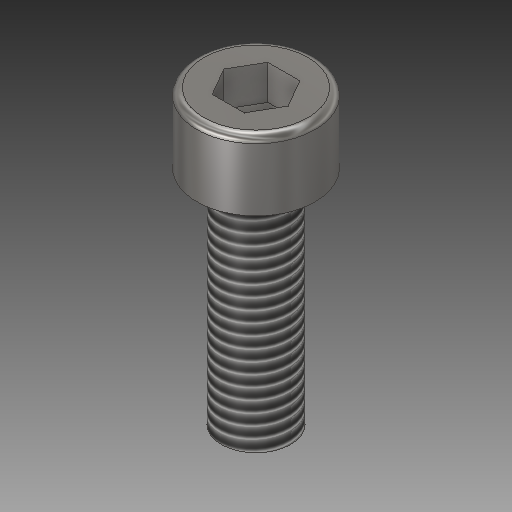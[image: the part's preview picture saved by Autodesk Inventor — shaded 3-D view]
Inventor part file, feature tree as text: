
AUTODESK INVENTOR PART (.ipt)
format: ipt  version: 2019 (Build 230136000, 136)  size: 172,032 bytes
history: native  units: mm
features: other x3, extrude x2, fillet x1
ambient origin geometry x8: Origin, YZ Plane, XZ Plane, XY Plane, X Axis, Y Axis, Z Axis, Center Point
bodies: Solid1 (feature_tree), Body (feature_tree)
feature tree (6):
  extrude  "Cap"  Depth=8.5mm
  extrude  "Key Socket Cutout"  Depth=5.0mm TaperAngle=0.0deg
  fillet  "Cap Fillet"  Radius=4.0mm
  other  "Cap Cross Section"
  other  "Key Socket Cutout Outline"
  other  "Body Cross Section"
